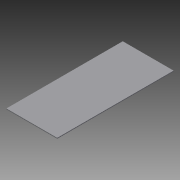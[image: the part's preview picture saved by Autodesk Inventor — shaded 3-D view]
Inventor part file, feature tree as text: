
AUTODESK INVENTOR PART (.ipt)
format: ipt  version: 2013 (Build 170138000, 138)  size: 66,048 bytes
history: native  units: mm
features: extrude x1, sketch x1
ambient origin geometry x8: Origin, YZ Plane, XZ Plane, XY Plane, X Axis, Y Axis, Z Axis, Center Point
bodies: Solid1 (feature_tree)
feature tree (2):
  extrude  "Extrusion1"  Depth=520.0mm
  sketch  "Sketch1"  dims[d0=1190.0mm d1=520.0mm d2=8.0mm d3=0.0mm]
